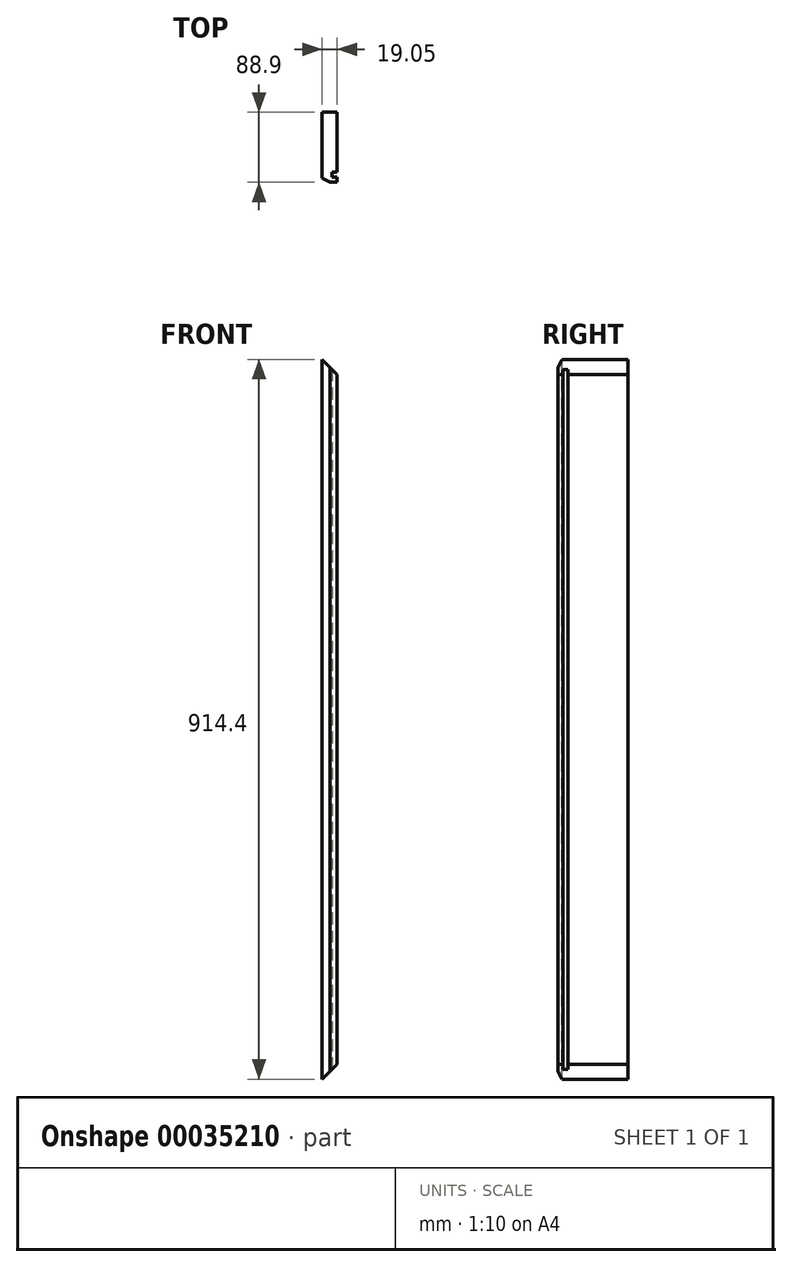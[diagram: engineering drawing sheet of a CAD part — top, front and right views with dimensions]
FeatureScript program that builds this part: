
annotation { "Feature Type Name" : "Feature", "Feature Type Description" : "" }
export const myFeature = defineFeature(function(context is Context, id is Id, definition is map)
    precondition{}
    {
        {
            var Q0;
            Q0=qCreatedBy(makeId("Right.planeOp"),FACE);
            var sketch = newSketch(context, id + "F0", { "sketchPlane" : qUnion([Q0])});
            skLineSegment(sketch, "E0.bottom", {"start": v(0, 0) * mm, "end": v(88.9, 0) * mm});
            skLineSegment(sketch, "E0.top", {"start": v(0, 914.4) * mm, "end": v(88.9, 914.4) * mm});
            skLineSegment(sketch, "E0.left", {"start": v(0, 0) * mm, "end": v(0, 914.4) * mm});
            skLineSegment(sketch, "E0.right", {"start": v(88.9, 0) * mm, "end": v(88.9, 914.4) * mm});
            skSolve(sketch);
        }
        {
            var Q0;
            Q0=makeQuery(id+"F0.imprint","IMPRINT",FACE,{"disambiguationData":[TD([[makeQuery(id+"F0.imprint","IMPRINT",EDGE,{"derivedFrom":sQuery(id+"F0.wireOp",EDGE,"E0.bottom")}),1.0]])]});
            extrude(context, id + "F1", {"entities" : qUnion([Q0]), "depth" : 19.05 * mm});
        }
        {
            var Q0;
            Q0=makeQuery(id+"F1.opExtrude","CAP_FACE",FACE,{"disambiguationData":[OSD([sQuery(id+"F0.wireOp",EDGE,"E0.bottom"),sQuery(id+"F0.wireOp",EDGE,"E0.top"),sQuery(id+"F0.wireOp",EDGE,"E0.left"),sQuery(id+"F0.wireOp",EDGE,"E0.right")])],"isStart":false});
            var sketch = newSketch(context, id + "F2", { "sketchPlane" : qUnion([Q0])});
            skLineSegment(sketch, "E1.bottom", {"start": v(6.35, 914.4) * mm, "end": v(12.7, 914.4) * mm});
            skLineSegment(sketch, "E1.top", {"start": v(6.35, 0) * mm, "end": v(12.7, 0) * mm});
            skLineSegment(sketch, "E1.left", {"start": v(6.35, 914.4) * mm, "end": v(6.35, 0) * mm});
            skLineSegment(sketch, "E1.right", {"start": v(12.7, 914.4) * mm, "end": v(12.7, 0) * mm});
            skSolve(sketch);
        }
        {
            var Q0;
            Q0 = qSketchRegion(id + "F2", true);
            extrude(context, id + "F3", {"entities" : qUnion([Q0]), "operationType" : NewBodyOperationType.REMOVE, "oppositeDirection" : true, "depth" : 6.35 * mm});
        }
        {
            var Q0;
            Q0=makeQuery(id+"F1.opExtrude","CAP_EDGE",EDGE,{"disambiguationData":[OSD([sQuery(id+"F0.wireOp",EDGE,"E0.left")])],"isStart":true});
            chamfer(context, id + "F4", {"entities" : qUnion([Q0]), "chamferType" : ChamferType.TWO_OFFSETS, "width1" : 10.16 * mm, "oppositeDirection" : true, "width2" : 5.08 * mm, "tangentPropagation" : true});
        }
        {
            var Q0;
            Q0=makeQuery(id+"F1.opExtrude","SWEPT_FACE",FACE,{"disambiguationData":[OSD([sQuery(id+"F0.wireOp",EDGE,"E0.right")])]});
            var sketch = newSketch(context, id + "F5", { "sketchPlane" : qUnion([Q0])});
            skLineSegment(sketch, "E2", {"start": v(0, 914.4) * mm, "end": v(-19.05, 895.35) * mm});
            skLineSegment(sketch, "E3", {"start": v(-19.05, 895.35) * mm, "end": v(-19.05, 914.4) * mm});
            skLineSegment(sketch, "E4", {"start": v(-19.05, 914.4) * mm, "end": v(0, 914.4) * mm});
            skLineSegment(sketch, "E5", {"start": v(0, 0) * mm, "end": v(-19.05, 19.05) * mm});
            skLineSegment(sketch, "E6", {"start": v(-19.05, 19.05) * mm, "end": v(-19.05, 0) * mm});
            skLineSegment(sketch, "E7", {"start": v(-19.05, 0) * mm, "end": v(0, 0) * mm});
            skSolve(sketch);
        }
        {
            var Q0;
            Q0 = qSketchRegion(id + "F5", true);
            extrude(context, id + "F6", {"entities" : qUnion([Q0]), "operationType" : NewBodyOperationType.REMOVE, "endBound" : BoundingType.THROUGH_ALL, "oppositeDirection" : true, "depth" : 25.4 * mm});
        }
    });
